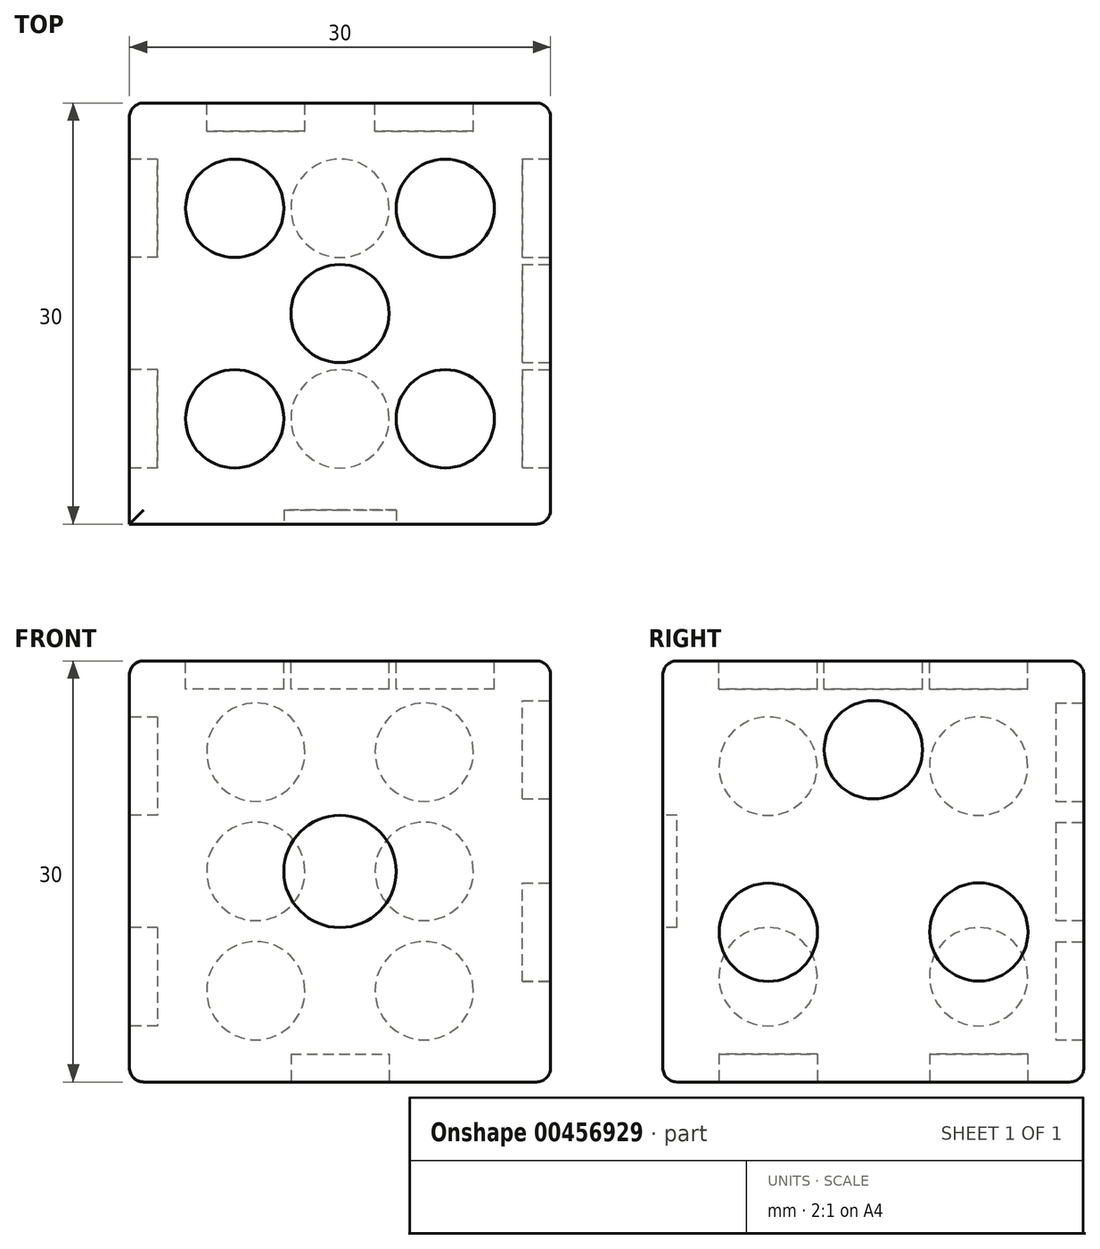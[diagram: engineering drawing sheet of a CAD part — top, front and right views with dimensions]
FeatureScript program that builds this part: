
annotation { "Feature Type Name" : "Feature", "Feature Type Description" : "" }
export const myFeature = defineFeature(function(context is Context, id is Id, definition is map)
    precondition{}
    {
        {
            var Q0;
            Q0=qCreatedBy(makeId("Top.planeOp"),FACE);
            var sketch = newSketch(context, id + "F0", { "sketchPlane" : qUnion([Q0])});
            skLineSegment(sketch, "E0.bottom", {"start": v(-15, 15) * mm, "end": v(15, 15) * mm});
            skLineSegment(sketch, "E0.top", {"start": v(-15, -15) * mm, "end": v(15, -15) * mm});
            skLineSegment(sketch, "E0.left", {"start": v(-15, 15) * mm, "end": v(-15, -15) * mm});
            skLineSegment(sketch, "E0.right", {"start": v(15, 15) * mm, "end": v(15, -15) * mm});
            skPoint(sketch, "E0.middle", {"position": v(0, 0) * mm});
            skSolve(sketch);
        }
        {
            var Q0;
            Q0=makeQuery(id+"F0.imprint","IMPRINT",FACE,{"disambiguationData":[TD([[makeQuery(id+"F0.imprint","IMPRINT",EDGE,{"derivedFrom":sQuery(id+"F0.wireOp",EDGE,"E0.bottom")}),-1.0]])]});
            extrude(context, id + "F1", {"entities" : qUnion([Q0]), "depth" : 15 * mm, "hasSecondDirection" : true, "secondDirectionOppositeDirection" : true, "secondDirectionDepth" : 15 * mm});
        }
        {
            var Q0;
            Q0=makeQuery(id+"F1.opExtrude","SWEPT_FACE",FACE,{"disambiguationData":[OSD([sQuery(id+"F0.wireOp",EDGE,"E0.top")])]});
            var sketch = newSketch(context, id + "F2", { "sketchPlane" : qUnion([Q0])});
            skCircle(sketch, "E1", {"center": v(0, 0) * mm, "radius": 4 * mm});
            skSolve(sketch);
        }
        {
            var Q0;
            Q0 = qSketchRegion(id + "F2", true);
            extrude(context, id + "F3", {"entities" : qUnion([Q0]), "operationType" : NewBodyOperationType.REMOVE, "oppositeDirection" : true, "depth" : 1 * mm});
        }
        {
            var Q0;
            Q0=makeQuery(id+"F1.opExtrude","SWEPT_FACE",FACE,{"disambiguationData":[OSD([sQuery(id+"F0.wireOp",EDGE,"E0.bottom")])]});
            var sketch = newSketch(context, id + "F4", { "sketchPlane" : qUnion([Q0])});
            skCircle(sketch, "E2", {"center": v(-6, 8.5) * mm, "radius": 3.5 * mm});
            skCircle(sketch, "E3", {"center": v(6, 8.5) * mm, "radius": 3.5 * mm});
            skCircle(sketch, "E4", {"center": v(-6, -8.5) * mm, "radius": 3.5 * mm});
            skCircle(sketch, "E5", {"center": v(6, -8.5) * mm, "radius": 3.5 * mm});
            skCircle(sketch, "E6", {"center": v(-6, 0) * mm, "radius": 3.5 * mm});
            skCircle(sketch, "E7", {"center": v(6, 0) * mm, "radius": 3.5 * mm});
            skSolve(sketch);
        }
        {
            var Q0;
            Q0=makeQuery(id+"F4.imprint","IMPRINT",FACE,{"disambiguationData":[TD([[makeQuery(id+"F4.imprint","IMPRINT",EDGE,{"derivedFrom":sQuery(id+"F4.wireOp",EDGE,"E2")}),1.0]])]});
            var Q1;
            Q1=makeQuery(id+"F4.imprint","IMPRINT",FACE,{"disambiguationData":[TD([[makeQuery(id+"F4.imprint","IMPRINT",EDGE,{"derivedFrom":sQuery(id+"F4.wireOp",EDGE,"E3")}),1.0]])]});
            var Q2;
            Q2=makeQuery(id+"F4.imprint","IMPRINT",FACE,{"disambiguationData":[TD([[makeQuery(id+"F4.imprint","IMPRINT",EDGE,{"derivedFrom":sQuery(id+"F4.wireOp",EDGE,"E7")}),1.0]])]});
            var Q3;
            Q3=makeQuery(id+"F4.imprint","IMPRINT",FACE,{"disambiguationData":[TD([[makeQuery(id+"F4.imprint","IMPRINT",EDGE,{"derivedFrom":sQuery(id+"F4.wireOp",EDGE,"E6")}),1.0]])]});
            var Q4;
            Q4=makeQuery(id+"F4.imprint","IMPRINT",FACE,{"disambiguationData":[TD([[makeQuery(id+"F4.imprint","IMPRINT",EDGE,{"derivedFrom":sQuery(id+"F4.wireOp",EDGE,"E5")}),1.0]])]});
            var Q5;
            Q5=makeQuery(id+"F4.imprint","IMPRINT",FACE,{"disambiguationData":[TD([[makeQuery(id+"F4.imprint","IMPRINT",EDGE,{"derivedFrom":sQuery(id+"F4.wireOp",EDGE,"E4")}),1.0]])]});
            extrude(context, id + "F5", {"entities" : qUnion([Q0, Q1, Q2, Q3, Q4, Q5]), "operationType" : NewBodyOperationType.REMOVE, "oppositeDirection" : true, "depth" : 2 * mm});
        }
        {
            var Q0;
            Q0=makeQuery(id+"F1.opExtrude","CAP_FACE",FACE,{"disambiguationData":[OSD([sQuery(id+"F0.wireOp",EDGE,"E0.bottom"),sQuery(id+"F0.wireOp",EDGE,"E0.top"),sQuery(id+"F0.wireOp",EDGE,"E0.left"),sQuery(id+"F0.wireOp",EDGE,"E0.right")])],"isStart":true});
            var sketch = newSketch(context, id + "F6", { "sketchPlane" : qUnion([Q0])});
            skCircle(sketch, "E8", {"center": v(0, -7.5) * mm, "radius": 3.5 * mm});
            skCircle(sketch, "E9", {"center": v(0, 7.5) * mm, "radius": 3.5 * mm});
            skSolve(sketch);
        }
        {
            var Q0;
            Q0=makeQuery(id+"F6.imprint","IMPRINT",FACE,{"disambiguationData":[TD([[makeQuery(id+"F6.imprint","IMPRINT",EDGE,{"derivedFrom":sQuery(id+"F6.wireOp",EDGE,"E8")}),1.0]])]});
            var Q1;
            Q1=makeQuery(id+"F6.imprint","IMPRINT",FACE,{"disambiguationData":[TD([[makeQuery(id+"F6.imprint","IMPRINT",EDGE,{"derivedFrom":sQuery(id+"F6.wireOp",EDGE,"E9")}),1.0]])]});
            extrude(context, id + "F7", {"entities" : qUnion([Q0, Q1]), "operationType" : NewBodyOperationType.REMOVE, "oppositeDirection" : true, "depth" : 2 * mm});
        }
        {
            var Q0;
            Q0=makeQuery(id+"F1.opExtrude","CAP_FACE",FACE,{"disambiguationData":[OSD([sQuery(id+"F0.wireOp",EDGE,"E0.bottom"),sQuery(id+"F0.wireOp",EDGE,"E0.top"),sQuery(id+"F0.wireOp",EDGE,"E0.left"),sQuery(id+"F0.wireOp",EDGE,"E0.right")])],"isStart":false});
            var sketch = newSketch(context, id + "F8", { "sketchPlane" : qUnion([Q0])});
            skPoint(sketch, "E10.0", {"position": v(-15, -15) * mm});
            skPoint(sketch, "E11.0", {"position": v(15, 15) * mm});
            skLineSegment(sketch, "E12", {"start": v(-15, -15) * mm, "end": v(15, 15) * mm, "construction": true});
            skPoint(sketch, "E13.0", {"position": v(-15, 15) * mm});
            skPoint(sketch, "E14.0", {"position": v(15, -15) * mm});
            skLineSegment(sketch, "E15", {"start": v(-15, 15) * mm, "end": v(15, -15) * mm, "construction": true});
            skCircle(sketch, "E16", {"center": v(0, 0) * mm, "radius": 3.5 * mm});
            skCircle(sketch, "E17", {"center": v(-7.5, 7.5) * mm, "radius": 3.5 * mm});
            skCircle(sketch, "E18", {"center": v(-7.5, -7.5) * mm, "radius": 3.5 * mm});
            skCircle(sketch, "E19", {"center": v(7.5, -7.5) * mm, "radius": 3.5 * mm});
            skCircle(sketch, "E20", {"center": v(7.5, 7.5) * mm, "radius": 3.5 * mm});
            skSolve(sketch);
        }
        {
            var Q0;
            Q0=makeQuery(id+"F8.imprint","IMPRINT",FACE,{"disambiguationData":[TD([[makeQuery(id+"F8.imprint","IMPRINT",EDGE,{"derivedFrom":sQuery(id+"F8.wireOp",EDGE,"E18")}),1.0]])]});
            var Q1;
            Q1=makeQuery(id+"F8.imprint","IMPRINT",FACE,{"disambiguationData":[TD([[makeQuery(id+"F8.imprint","IMPRINT",EDGE,{"derivedFrom":sQuery(id+"F8.wireOp",EDGE,"E17")}),1.0]])]});
            var Q2;
            Q2=makeQuery(id+"F8.imprint","IMPRINT",FACE,{"disambiguationData":[TD([[makeQuery(id+"F8.imprint","IMPRINT",EDGE,{"derivedFrom":sQuery(id+"F8.wireOp",EDGE,"E16")}),1.0]])]});
            var Q3;
            Q3=makeQuery(id+"F8.imprint","IMPRINT",FACE,{"disambiguationData":[TD([[makeQuery(id+"F8.imprint","IMPRINT",EDGE,{"derivedFrom":sQuery(id+"F8.wireOp",EDGE,"E20")}),1.0]])]});
            var Q4;
            Q4=makeQuery(id+"F8.imprint","IMPRINT",FACE,{"disambiguationData":[TD([[makeQuery(id+"F8.imprint","IMPRINT",EDGE,{"derivedFrom":sQuery(id+"F8.wireOp",EDGE,"E19")}),1.0]])]});
            extrude(context, id + "F9", {"entities" : qUnion([Q0, Q1, Q2, Q3, Q4]), "operationType" : NewBodyOperationType.REMOVE, "oppositeDirection" : true, "depth" : 2 * mm});
        }
        {
            var Q0;
            Q0=makeQuery(id+"F1.opExtrude","SWEPT_FACE",FACE,{"disambiguationData":[OSD([sQuery(id+"F0.wireOp",EDGE,"E0.left")])]});
            var sketch = newSketch(context, id + "F10", { "sketchPlane" : qUnion([Q0])});
            skLineSegment(sketch, "E21", {"start": v(15, -15) * mm, "end": v(-15, 15) * mm, "construction": true});
            skLineSegment(sketch, "E22", {"start": v(-15, -15) * mm, "end": v(15, 15) * mm, "construction": true});
            skCircle(sketch, "E23", {"center": v(7.5, -7.5) * mm, "radius": 3.5 * mm});
            skCircle(sketch, "E24", {"center": v(-7.5, -7.5) * mm, "radius": 3.5 * mm});
            skCircle(sketch, "E25", {"center": v(7.5, 7.5) * mm, "radius": 3.5 * mm});
            skCircle(sketch, "E26", {"center": v(-7.5, 7.5) * mm, "radius": 3.5 * mm});
            skSolve(sketch);
        }
        {
            var Q0;
            Q0=makeQuery(id+"F10.imprint","IMPRINT",FACE,{"disambiguationData":[TD([[makeQuery(id+"F10.imprint","IMPRINT",EDGE,{"derivedFrom":sQuery(id+"F10.wireOp",EDGE,"E23")}),1.0]])]});
            var Q1;
            Q1=makeQuery(id+"F10.imprint","IMPRINT",FACE,{"disambiguationData":[TD([[makeQuery(id+"F10.imprint","IMPRINT",EDGE,{"derivedFrom":sQuery(id+"F10.wireOp",EDGE,"E24")}),1.0]])]});
            var Q2;
            Q2=makeQuery(id+"F10.imprint","IMPRINT",FACE,{"disambiguationData":[TD([[makeQuery(id+"F10.imprint","IMPRINT",EDGE,{"derivedFrom":sQuery(id+"F10.wireOp",EDGE,"E25")}),1.0]])]});
            var Q3;
            Q3=makeQuery(id+"F10.imprint","IMPRINT",FACE,{"disambiguationData":[TD([[makeQuery(id+"F10.imprint","IMPRINT",EDGE,{"derivedFrom":sQuery(id+"F10.wireOp",EDGE,"E26")}),1.0]])]});
            extrude(context, id + "F11", {"entities" : qUnion([Q0, Q1, Q2, Q3]), "operationType" : NewBodyOperationType.REMOVE, "oppositeDirection" : true, "depth" : 2 * mm});
        }
        {
            var Q0;
            Q0=makeQuery(id+"F1.opExtrude","SWEPT_FACE",FACE,{"disambiguationData":[OSD([sQuery(id+"F0.wireOp",EDGE,"E0.right")])]});
            var sketch = newSketch(context, id + "F12", { "sketchPlane" : qUnion([Q0])});
            skCircle(sketch, "E27", {"center": v(0, 8.67) * mm, "radius": 3.5 * mm});
            skCircle(sketch, "E28", {"center": v(-7.48, -4.33) * mm, "radius": 3.5 * mm});
            skCircle(sketch, "E29", {"center": v(7.52, -4.31) * mm, "radius": 3.5 * mm});
            skSolve(sketch);
        }
        {
            var Q0;
            Q0=makeQuery(id+"F12.imprint","IMPRINT",FACE,{"disambiguationData":[TD([[makeQuery(id+"F12.imprint","IMPRINT",EDGE,{"derivedFrom":sQuery(id+"F12.wireOp",EDGE,"E27")}),1.0]])]});
            var Q1;
            Q1=makeQuery(id+"F12.imprint","IMPRINT",FACE,{"disambiguationData":[TD([[makeQuery(id+"F12.imprint","IMPRINT",EDGE,{"derivedFrom":sQuery(id+"F12.wireOp",EDGE,"E28")}),1.0]])]});
            var Q2;
            Q2=makeQuery(id+"F12.imprint","IMPRINT",FACE,{"disambiguationData":[TD([[makeQuery(id+"F12.imprint","IMPRINT",EDGE,{"derivedFrom":sQuery(id+"F12.wireOp",EDGE,"E29")}),1.0]])]});
            extrude(context, id + "F13", {"entities" : qUnion([Q0, Q1, Q2]), "operationType" : NewBodyOperationType.REMOVE, "oppositeDirection" : true, "depth" : 2 * mm});
        }
        {
            var Q0;
            Q0=makeQuery(id+"F1.opExtrude","CAP_EDGE",EDGE,{"disambiguationData":[OSD([sQuery(id+"F0.wireOp",EDGE,"E0.bottom")])],"isStart":false});
            var Q1;
            Q1=makeQuery(id+"F1.opExtrude","SWEPT_EDGE",EDGE,{"disambiguationData":[OSD([sQuery(id+"F0.wireOp",EDGE,"E0.bottom"),sQuery(id+"F0.wireOp",EDGE,"E0.right")])]});
            var Q2;
            Q2=makeQuery(id+"F1.opExtrude","CAP_EDGE",EDGE,{"disambiguationData":[OSD([sQuery(id+"F0.wireOp",EDGE,"E0.bottom")])],"isStart":true});
            var Q3;
            Q3=makeQuery(id+"F1.opExtrude","SWEPT_EDGE",EDGE,{"disambiguationData":[OSD([sQuery(id+"F0.wireOp",EDGE,"E0.bottom"),sQuery(id+"F0.wireOp",EDGE,"E0.left")])]});
            var Q4;
            Q4=makeQuery(id+"F1.opExtrude","CAP_EDGE",EDGE,{"disambiguationData":[OSD([sQuery(id+"F0.wireOp",EDGE,"E0.left")])],"isStart":true});
            var Q5;
            Q5=makeQuery(id+"F1.opExtrude","CAP_EDGE",EDGE,{"disambiguationData":[OSD([sQuery(id+"F0.wireOp",EDGE,"E0.right")])],"isStart":true});
            var Q6;
            Q6=makeQuery(id+"F1.opExtrude","SWEPT_EDGE",EDGE,{"disambiguationData":[OSD([sQuery(id+"F0.wireOp",EDGE,"E0.top"),sQuery(id+"F0.wireOp",EDGE,"E0.right")])]});
            var Q7;
            Q7=makeQuery(id+"F1.opExtrude","CAP_EDGE",EDGE,{"disambiguationData":[OSD([sQuery(id+"F0.wireOp",EDGE,"E0.right")])],"isStart":false});
            var Q8;
            Q8=makeQuery(id+"F1.opExtrude","CAP_EDGE",EDGE,{"disambiguationData":[OSD([sQuery(id+"F0.wireOp",EDGE,"E0.left")])],"isStart":false});
            var Q9;
            Q9=makeQuery(id+"F1.opExtrude","CAP_EDGE",EDGE,{"disambiguationData":[OSD([sQuery(id+"F0.wireOp",EDGE,"E0.top")])],"isStart":false});
            var Q10;
            Q10=makeQuery(id+"F1.opExtrude","CAP_EDGE",EDGE,{"disambiguationData":[OSD([sQuery(id+"F0.wireOp",EDGE,"E0.top")])],"isStart":true});
            fillet(context, id + "F14", {"entities" : qUnion([Q0, Q1, Q2, Q3, Q4, Q5, Q6, Q7, Q8, Q9, Q10]), "radius" : 1 * mm, "tangentPropagation" : true, "allowEdgeOverflow" : false});
        }
    });
